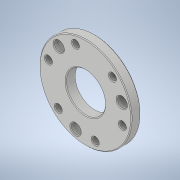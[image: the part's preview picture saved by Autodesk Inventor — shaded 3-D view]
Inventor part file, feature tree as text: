
AUTODESK INVENTOR PART (.ipt)
format: ipt  version: 2021 (Build 250183000, 183)  size: 174,592 bytes
history: native  units: in
note: dims shown in document units (in); Inventor stores cm internally (conversion verified against a paired STEP export)
features: sketch x3, extrude x2, revolve x1, chamfer x1
ambient origin geometry x8: Origin, YZ Plane, XZ Plane, XY Plane, X Axis, Y Axis, Z Axis, Center Point
bodies: Solid1 (feature_tree)
feature tree (7):
  revolve  "Revolution1"  [1 undecoded]
  extrude  "Extrusion1"  Depth=3.078in
  extrude  "Extrusion2"  Depth=0.375in
  chamfer  "Chamfer1"  Distance=2.3622in Angle=360.0deg
  sketch  "Sketch1"  dims[d0=1.8505in d1=0.375in]
  sketch  "Sketch2"  dims[d2=90.0deg d3=3.078in]
  sketch  "Sketch3"  dims[d4=45.0deg d5=0.268in d6=2.3622in d8=360.0deg d10=0.375in d11=0.0in d12=3.03in d13=135.0deg d14=0.4in d15=1.1811in d17=360.0deg d19=0.375in d20=0.0in d21=1.57in d22=0.03in d23=0.125in d24=45.0deg]
note: 1 required parameter value undecoded (feature->parameter linkage not recoverable at this tier; creation-order binding heuristic only, values carry confidence <= 0.55)
